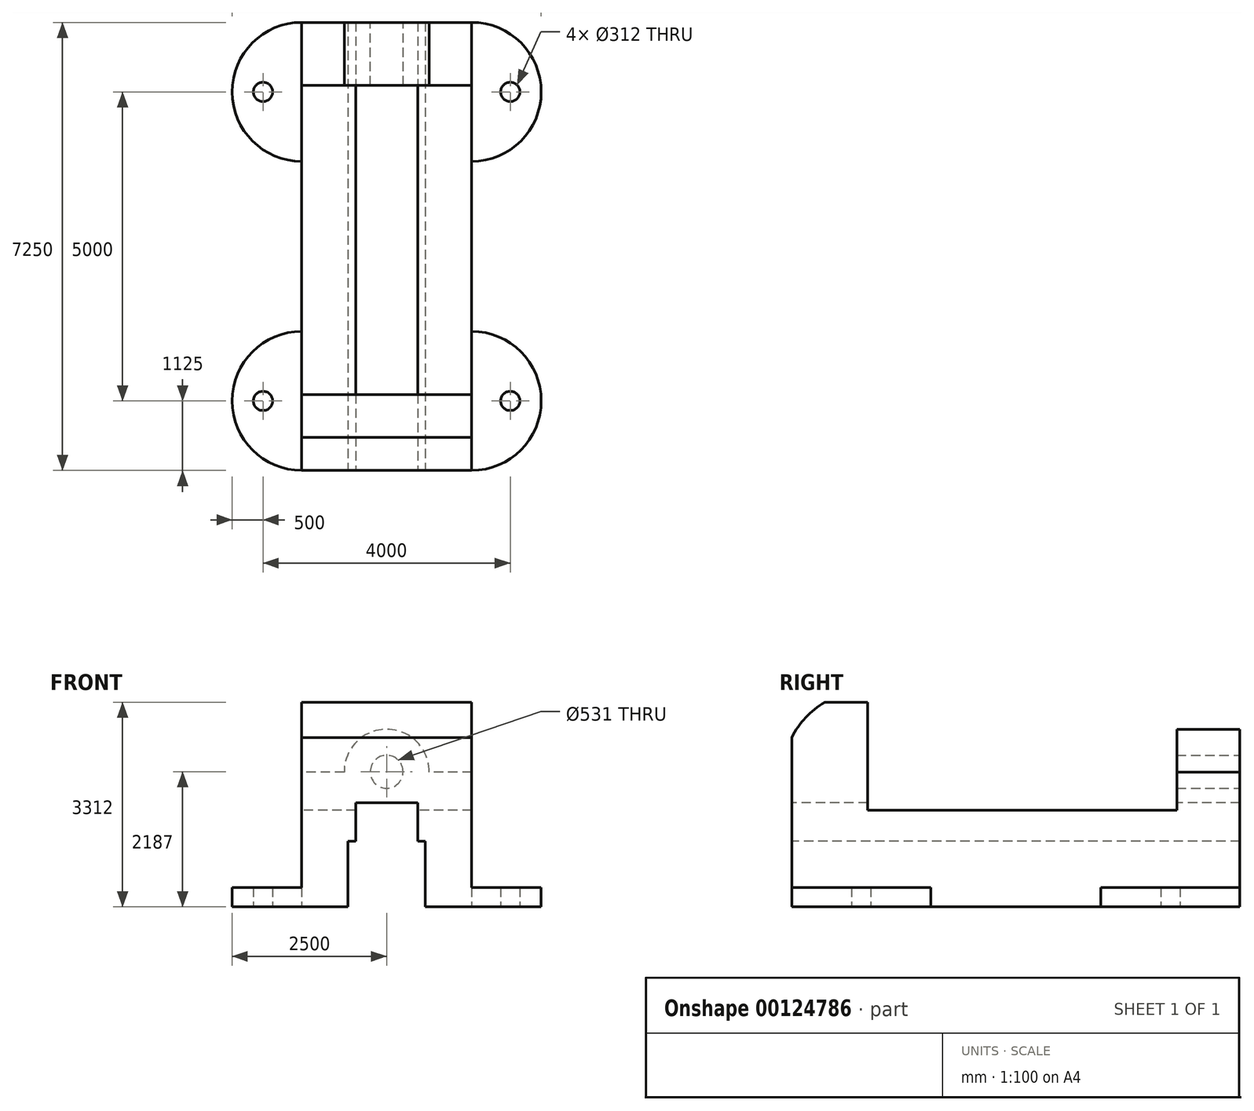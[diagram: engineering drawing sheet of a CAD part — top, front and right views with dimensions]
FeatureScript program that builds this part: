
annotation { "Feature Type Name" : "Feature", "Feature Type Description" : "" }
export const myFeature = defineFeature(function(context is Context, id is Id, definition is map)
    precondition{}
    {
        {
            var Q0;
            Q0=qCreatedBy(makeId("Right.planeOp"),FACE);
            var sketch = newSketch(context, id + "F0", { "sketchPlane" : qUnion([Q0])});
            skPoint(sketch, "E0.middle", {"position": v(0, 0) * mm});
            skLineSegment(sketch, "E1.bottom", {"start": v(-3089.01, 1656) * mm, "end": v(-2395, 1656) * mm});
            skLineSegment(sketch, "E1.top", {"start": v(-3625, -1656) * mm, "end": v(3625, -1656) * mm});
            skLineSegment(sketch, "E1.left", {"start": v(-3625, 1083.6) * mm, "end": v(-3625, -1656) * mm});
            skLineSegment(sketch, "E1.right", {"start": v(3625, 1656) * mm, "end": v(3625, -1656) * mm});
            skLineSegment(sketch, "E2.bottom", {"start": v(0, -11156.74) * mm, "end": v(0, -11156.74) * mm});
            skLineSegment(sketch, "E2.top", {"start": v(0, 11156.74) * mm, "end": v(0, 11156.74) * mm});
            skLineSegment(sketch, "E2.left", {"start": v(0, -11156.74) * mm, "end": v(0, 11156.74) * mm});
            skLineSegment(sketch, "E2.right", {"start": v(0, -11156.74) * mm, "end": v(0, -1656) * mm});
            skLineSegment(sketch, "E3", {"start": v(-2395, 1656) * mm, "end": v(-2395, -94) * mm});
            skLineSegment(sketch, "E4", {"start": v(2605, 1656) * mm, "end": v(2605, -94) * mm});
            skLineSegment(sketch, "E5.trimOffspring", {"start": v(-2395, -94) * mm, "end": v(2605, -94) * mm});
            skPoint(sketch, "E6.orphan", {"position": v(-2395, -2164) * mm});
            skPoint(sketch, "E7.trimOffspring.end.orphan", {"position": v(2605, -2164) * mm});
            skLineSegment(sketch, "E8.trimOffspring", {"start": v(0, -94) * mm, "end": v(0, 1656) * mm});
            skPoint(sketch, "E9.visualSharp", {"position": v(-3625, 1656) * mm});
            skArc(sketch, "E9.filletArc", {"start": v(-3623.62, 1656) * mm, "mid": v(-3624.6, 1655.6) * mm, "end": v(-3625, 1654.62) * mm});
            skLineSegment(sketch, "E10", {"start": v(246138.83, -183456.89) * mm, "end": v(245486.44, -181323.03) * mm});
            skArc(sketch, "E11", {"start": v(-3089.01, 1656) * mm, "mid": v(-3398.68, 1408.82) * mm, "end": v(-3625, 1083.6) * mm});
            skLineSegment(sketch, "E12.trimOffspring", {"start": v(2605, 1656) * mm, "end": v(3625, 1656) * mm});
            skSolve(sketch);
        }
        {
            var Q0;
            Q0=makeQuery(id+"F0.imprint","IMPRINT",FACE,{"disambiguationData":[TD([[makeQuery(id+"F0.imprint","IMPRINT",EDGE,{"derivedFrom":sQuery(id+"F0.wireOp",EDGE,"E1.bottom")}),-1.0]])]});
            var Q1;
            {var subQ0=sQuery(id+"F0.wireOp",EDGE,"E1.right");Q1=makeQuery(id+"F0.imprint","IMPRINT",FACE,{"disambiguationData":[TD([[makeQuery(id+"F0.imprint","IMPRINT",EDGE,{"derivedFrom":subQ0}),-1.0]])]});}
            extrude(context, id + "F1", {"entities" : qUnion([Q0, Q1]), "depth" : 2750 * mm});
        }
        {
            var Q0;
            Q0=makeQuery(id+"F1.opExtrude","SWEPT_FACE",FACE,{"disambiguationData":[OSD([sQuery(id+"F0.wireOp",EDGE,"E1.top")])]});
            var sketch = newSketch(context, id + "F2", { "sketchPlane" : qUnion([Q0])});
            skCircle(sketch, "E13", {"center": v(0, 2500) * mm, "radius": 1125 * mm});
            skCircle(sketch, "E14", {"center": v(2750, 2500) * mm, "radius": 1125 * mm});
            skCircle(sketch, "E15", {"center": v(2750, -2500) * mm, "radius": 1125 * mm});
            skCircle(sketch, "E16", {"center": v(0, -2500) * mm, "radius": 1125 * mm});
            skCircle(sketch, "E17", {"center": v(-625, 2500) * mm, "radius": 156 * mm});
            skCircle(sketch, "E18", {"center": v(3375, 2500) * mm, "radius": 156 * mm});
            skCircle(sketch, "E19", {"center": v(3375, -2500) * mm, "radius": 156 * mm});
            skCircle(sketch, "E20", {"center": v(-625, -2500) * mm, "radius": 156 * mm});
            skSolve(sketch);
        }
        {
            var Q0;
            Q0 = qSketchRegion(id + "F2", true);
            extrude(context, id + "F3", {"entities" : qUnion([Q0]), "operationType" : NewBodyOperationType.ADD, "oppositeDirection" : true, "depth" : 312 * mm});
        }
        {
            var Q0;
            Q0=makeQuery(id+"F1.opExtrude","SWEPT_FACE",FACE,{"disambiguationData":[OSD([sQuery(id+"F0.wireOp",EDGE,"E1.left")])]});
            var sketch = newSketch(context, id + "F4", { "sketchPlane" : qUnion([Q0])});
            skLineSegment(sketch, "E21.bottom", {"start": v(875, 32) * mm, "end": v(1875, 32) * mm});
            skLineSegment(sketch, "E21.top", {"start": v(875, -1656) * mm, "end": v(1875, -1656) * mm});
            skLineSegment(sketch, "E21.left", {"start": v(875, 32) * mm, "end": v(875, -594) * mm});
            skLineSegment(sketch, "E21.right", {"start": v(1875, 32) * mm, "end": v(1875, -594) * mm});
            skLineSegment(sketch, "E22", {"start": v(1375, 32) * mm, "end": v(1375, 3043.88) * mm});
            skPoint(sketch, "E22.endSnap0", {"position": v(1375, 1083.6) * mm});
            skPoint(sketch, "E23.middle", {"position": v(1375, -1656) * mm});
            skLineSegment(sketch, "E24.bottom", {"start": v(750, -594) * mm, "end": v(875, -594) * mm});
            skLineSegment(sketch, "E24.top", {"start": v(750, -1656) * mm, "end": v(2000, -1656) * mm});
            skLineSegment(sketch, "E24.left", {"start": v(750, -594) * mm, "end": v(750, -1656) * mm});
            skLineSegment(sketch, "E24.right", {"start": v(2000, -594) * mm, "end": v(2000, -1656) * mm});
            skPoint(sketch, "E24.middle", {"position": v(1375, -1125) * mm});
            skLineSegment(sketch, "E25.trimOffspring", {"start": v(1875, -594) * mm, "end": v(2000, -594) * mm});
            skSolve(sketch);
        }
        {
            var Q0;
            Q0 = qSketchRegion(id + "F4", true);
            extrude(context, id + "F5", {"entities" : qUnion([Q0]), "operationType" : NewBodyOperationType.REMOVE, "oppositeDirection" : true, "depth" : 9516.5 * mm});
        }
        {
            var Q0;
            Q0=makeQuery(id+"F1.opExtrude","SWEPT_FACE",FACE,{"disambiguationData":[OSD([sQuery(id+"F0.wireOp",EDGE,"E1.right")])]});
            var sketch = newSketch(context, id + "F6", { "sketchPlane" : qUnion([Q0])});
            skCircle(sketch, "E26", {"center": v(-1375, 531) * mm, "radius": 265.5 * mm});
            skArc(sketch, "E27", {"start": v(-688.03, 524.97) * mm, "mid": v(-1375, 1218) * mm, "end": v(-2061.97, 524.97) * mm});
            skLineSegment(sketch, "E28", {"start": v(-2750, 524.97) * mm, "end": v(-2061.97, 524.97) * mm});
            skLineSegment(sketch, "E29.trimOffspring", {"start": v(-688.03, 524.97) * mm, "end": v(0, 524.97) * mm});
            skSolve(sketch);
        }
        {
            var Q0;
            Q0 = qSketchRegion(id + "F6", true);
            var Q1;
            Q1=makeQuery(id+"F6.imprint","IMPRINT",FACE,{"disambiguationData":[TD([[makeQuery(id+"F6.imprint","IMPRINT",EDGE,{"derivedFrom":sQuery(id+"F6.wireOp",EDGE,"E27")}),-1.0]])]});
            extrude(context, id + "F7", {"entities" : qUnion([Q0, Q1]), "operationType" : NewBodyOperationType.REMOVE, "oppositeDirection" : true, "depth" : 2759.03 * mm});
        }
    });
